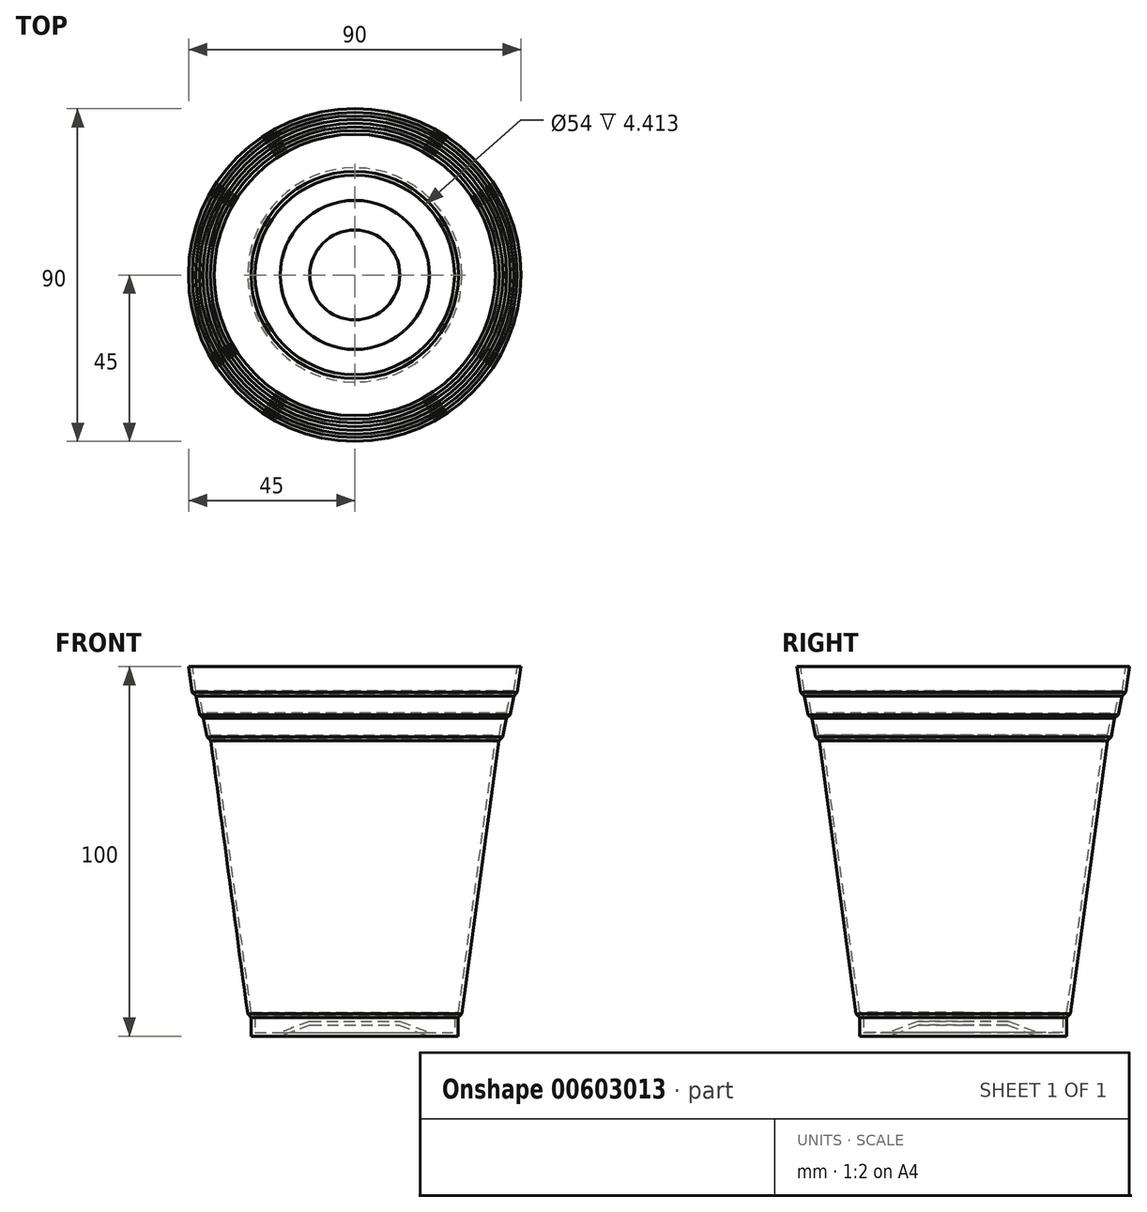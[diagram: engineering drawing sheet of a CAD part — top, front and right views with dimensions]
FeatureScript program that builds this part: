
annotation { "Feature Type Name" : "Feature", "Feature Type Description" : "" }
export const myFeature = defineFeature(function(context is Context, id is Id, definition is map)
    precondition{}
    {
        {
            var Q0;
            Q0=qCreatedBy(makeId("Front.planeOp"),FACE);
            var sketch = newSketch(context, id + "F0", { "sketchPlane" : qUnion([Q0])});
            skLineSegment(sketch, "E0", {"start": v(0, 0) * mm, "end": v(0, 3) * mm, "construction": true});
            skLineSegment(sketch, "E1", {"start": v(0, 3) * mm, "end": v(-12, 3) * mm});
            skLineSegment(sketch, "E2", {"start": v(0, 0) * mm, "end": v(-20, 0) * mm, "construction": true});
            skLineSegment(sketch, "E3", {"start": v(-20, 0) * mm, "end": v(-28, 0) * mm});
            skLineSegment(sketch, "E4", {"start": v(-12, 3) * mm, "end": v(-20, 0) * mm});
            skLineSegment(sketch, "E5", {"start": v(0, 0) * mm, "end": v(0, 100) * mm, "construction": true});
            skPoint(sketch, "E5.endSnap0", {"position": v(0, 1.5) * mm});
            skLineSegment(sketch, "E6", {"start": v(0, 100) * mm, "end": v(-45, 100) * mm});
            skLineSegment(sketch, "E7", {"start": v(0, 0) * mm, "end": v(0, 6) * mm, "construction": true});
            skLineSegment(sketch, "E8", {"start": v(0, 6) * mm, "end": v(-29, 6) * mm});
            skLineSegment(sketch, "E9", {"start": v(0, 0) * mm, "end": v(0, 93) * mm, "construction": true});
            skLineSegment(sketch, "E10", {"start": v(0, 93) * mm, "end": v(-44, 93) * mm});
            skLineSegment(sketch, "E11", {"start": v(-45, 100) * mm, "end": v(-44, 93) * mm});
            skLineSegment(sketch, "E12", {"start": v(0, 0) * mm, "end": v(0, 92) * mm, "construction": true});
            skLineSegment(sketch, "E13", {"start": v(0, 92) * mm, "end": v(-43, 92) * mm});
            skLineSegment(sketch, "E14", {"start": v(-43, 92) * mm, "end": v(-44, 93) * mm});
            skLineSegment(sketch, "E15", {"start": v(0, 0) * mm, "end": v(0, 87) * mm, "construction": true});
            skLineSegment(sketch, "E16", {"start": v(0, 87) * mm, "end": v(-42, 87) * mm});
            skLineSegment(sketch, "E17", {"start": v(-43, 92) * mm, "end": v(-42, 87) * mm});
            skLineSegment(sketch, "E18", {"start": v(0, 0) * mm, "end": v(0, 86) * mm, "construction": true});
            skLineSegment(sketch, "E19", {"start": v(0, 86) * mm, "end": v(-41, 86) * mm});
            skLineSegment(sketch, "E20", {"start": v(-42, 87) * mm, "end": v(-41, 86) * mm});
            skLineSegment(sketch, "E21", {"start": v(0, 0) * mm, "end": v(0, 81) * mm, "construction": true});
            skLineSegment(sketch, "E22", {"start": v(0, 81) * mm, "end": v(-40, 81) * mm});
            skLineSegment(sketch, "E23", {"start": v(-41, 86) * mm, "end": v(-40, 81) * mm});
            skLineSegment(sketch, "E24", {"start": v(0, 0) * mm, "end": v(0, 80) * mm, "construction": true});
            skLineSegment(sketch, "E25", {"start": v(0, 80) * mm, "end": v(-39, 80) * mm});
            skLineSegment(sketch, "E26", {"start": v(-40, 81) * mm, "end": v(-39, 80) * mm});
            skLineSegment(sketch, "E27", {"start": v(-39, 80) * mm, "end": v(-29, 6) * mm});
            skLineSegment(sketch, "E28", {"start": v(0, 0) * mm, "end": v(0, 5) * mm, "construction": true});
            skLineSegment(sketch, "E29", {"start": v(0, 5) * mm, "end": v(-28, 5) * mm});
            skLineSegment(sketch, "E30", {"start": v(-29, 6) * mm, "end": v(-28, 5) * mm});
            skLineSegment(sketch, "E31", {"start": v(-28, 5) * mm, "end": v(-28, 0) * mm});
            skLineSegment(sketch, "E32", {"start": v(0, 100) * mm, "end": v(0, 0) * mm});
            skSolve(sketch);
        }
        {
            var Q0;
            Q0=qCreatedBy(makeId("Front.planeOp"),FACE);
            var sketch = newSketch(context, id + "F1", { "sketchPlane" : qUnion([Q0])});
            skLineSegment(sketch, "E33", {"start": v(0, 0) * mm, "end": v(0, 115.54) * mm, "construction": true});
            skSolve(sketch);
        }
        {
            var Q0;
            Q0 = qSketchRegion(id + "F0", true);
            var Q1;
            Q1=sQuery(id+"F1.wireOp",EDGE,"E33");
            revolve(context, id + "F2", {"entities" : qUnion([Q0]), "axis" : qUnion([Q1]), "revolveType" : RevolveType.FULL});
        }
        {
            var Q0;
            Q0=makeQuery(id+"F2.opRevolve","SWEPT_FACE",FACE,{"disambiguationData":[OSD([sQuery(id+"F0.wireOp",EDGE,"E6")])]});
            shell(context, id + "F3", {"entities" : qUnion([Q0]), "thickness" : 1 * mm});
        }
    });
